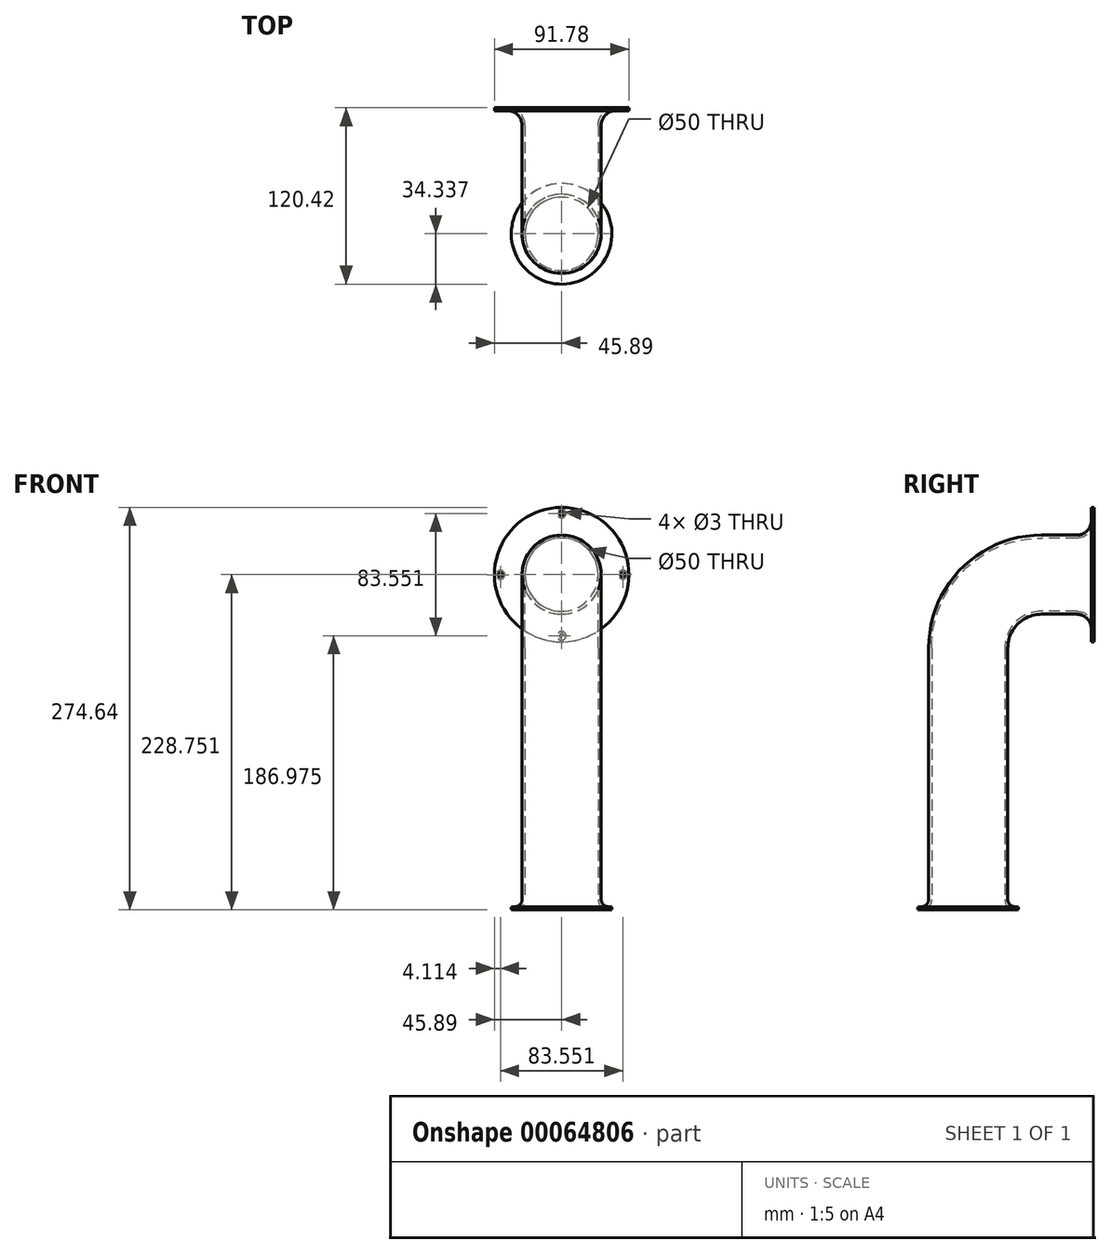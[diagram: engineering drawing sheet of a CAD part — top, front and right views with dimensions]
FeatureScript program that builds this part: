
annotation { "Feature Type Name" : "Feature", "Feature Type Description" : "" }
export const myFeature = defineFeature(function(context is Context, id is Id, definition is map)
    precondition{}
    {
        {
            var Q0;
            Q0=qCreatedBy(makeId("Right.planeOp"),FACE);
            var sketch = newSketch(context, id + "F0", { "sketchPlane" : qUnion([Q0])});
            skLineSegment(sketch, "E0", {"start": v(113.42, 188.16) * mm, "end": v(93.42, 188.16) * mm});
            skLineSegment(sketch, "E1", {"start": v(43.42, 138.16) * mm, "end": v(43.42, -31.84) * mm});
            skPoint(sketch, "E2.visualSharp", {"position": v(43.42, 188.16) * mm});
            skArc(sketch, "E2.filletArc", {"start": v(93.42, 188.16) * mm, "mid": v(58.06, 173.52) * mm, "end": v(43.42, 138.16) * mm});
            skSolve(sketch);
        }
        {
            var Q0;
            Q0=sQuery(id+"F0.wireOp",VERTEX,"E0.start");
            var Q1;
            Q1=sQuery(id+"F0.wireOp",EDGE,"E0");
            cPlane(context, id + "F1", {"entities" : qUnion([Q0, Q1]), "cplaneType" : CPlaneType.LINE_POINT, "offset" : 150 * mm, "width" : 150 * mm, "height" : 150 * mm});
        }
        {
            var Q0;
            Q0=qCreatedBy(id+"F1.planeOp",FACE);
            var sketch = newSketch(context, id + "F2", { "sketchPlane" : qUnion([Q0])});
            skCircle(sketch, "E3", {"center": v(0, 188.16) * mm, "radius": 25 * mm});
            skCircle(sketch, "E4", {"center": v(0, 188.16) * mm, "radius": 27 * mm});
            skPoint(sketch, "E5", {"position": v(0, 163.16) * mm});
            skPoint(sketch, "E6", {"position": v(0, 213.16) * mm});
            skPoint(sketch, "E7", {"position": v(-25, 188.16) * mm});
            skPoint(sketch, "E8", {"position": v(25, 188.16) * mm});
            skPoint(sketch, "E9", {"position": v(-27, 188.16) * mm});
            skPoint(sketch, "E10", {"position": v(27, 188.16) * mm});
            skSolve(sketch);
        }
        {
            var Q0;
            Q0=makeQuery(id+"F2.imprint","IMPRINT",FACE,{"disambiguationData":[TD([[makeQuery(id+"F2.imprint","IMPRINT",EDGE,{"derivedFrom":sQuery(id+"F2.wireOp",EDGE,"E3")}),-1.0]])]});
            var Q1;
            Q1=sQuery(id+"F0.wireOp",EDGE,"E0");
            var Q2;
            Q2=sQuery(id+"F0.wireOp",EDGE,"E2.filletArc");
            var Q3;
            Q3=sQuery(id+"F0.wireOp",EDGE,"E1");
            sweep(context, id + "F3", {"profiles" : qUnion([Q0]), "path" : qUnion([Q1, Q2, Q3])});
        }
        {
            var Q0;
            Q0=sQuery(id+"F2.wireOp",VERTEX,"E5");
            var Q1;
            Q1=sQuery(id+"F2.wireOp",VERTEX,"E6");
            cPlane(context, id + "F4", {"entities" : qUnion([Q0, Q1]), "cplaneType" : CPlaneType.MID_PLANE, "offset" : 150 * mm, "width" : 150 * mm, "height" : 150 * mm});
        }
        {
            var Q0;
            Q0=qCreatedBy(id+"F4.planeOp",FACE);
            var sketch = newSketch(context, id + "F5", { "sketchPlane" : qUnion([Q0])});
            skLineSegment(sketch, "E11", {"start": v(-27, 113.42) * mm, "end": v(-25, 113.42) * mm});
            skLineSegment(sketch, "E12", {"start": v(-27, 113.42) * mm, "end": v(-27, 117.5) * mm});
            skLineSegment(sketch, "E13", {"start": v(-37, 127.5) * mm, "end": v(-38.4, 127.5) * mm});
            skPoint(sketch, "E14.visualSharp", {"position": v(-27, 127.5) * mm});
            skArc(sketch, "E14.filletArc", {"start": v(-27, 117.5) * mm, "mid": v(-29.93, 124.57) * mm, "end": v(-37, 127.5) * mm});
            skArc(sketch, "E15.0", {"start": v(-25, 117.5) * mm, "mid": v(-28.51, 125.98) * mm, "end": v(-37, 129.5) * mm});
            skLineSegment(sketch, "E15.1", {"start": v(-25, 113.42) * mm, "end": v(-25, 117.5) * mm});
            skLineSegment(sketch, "E16", {"start": v(-37, 129.5) * mm, "end": v(-45.9, 129.5) * mm});
            skLineSegment(sketch, "E17", {"start": v(-45.9, 129.5) * mm, "end": v(-45.9, 127.5) * mm});
            skLineSegment(sketch, "E18", {"start": v(-45.9, 127.5) * mm, "end": v(-38.4, 127.5) * mm});
            skLineSegment(sketch, "E19", {"start": v(0, 126.02) * mm, "end": v(0, 107.88) * mm, "construction": true});
            skSolve(sketch);
        }
        {
            var Q0;
            Q0=makeQuery(id+"F5.imprint","IMPRINT",FACE,{"disambiguationData":[TD([[makeQuery(id+"F5.imprint","IMPRINT",EDGE,{"derivedFrom":sQuery(id+"F5.wireOp",EDGE,"E11")}),1.0]])]});
            var Q1;
            Q1=sQuery(id+"F5.wireOp",EDGE,"E19");
            revolve(context, id + "F6", {"operationType" : NewBodyOperationType.ADD, "entities" : qUnion([Q0]), "axis" : qUnion([Q1]), "revolveType" : RevolveType.FULL});
        }
        {
            var Q0;
            Q0=makeQuery(id+"F6.opRevolve","SWEPT_FACE",FACE,{"disambiguationData":[OSD([sQuery(id+"F5.wireOp",EDGE,"E16")])]});
            var sketch = newSketch(context, id + "F7", { "sketchPlane" : qUnion([Q0])});
            skCircle(sketch, "E20", {"center": v(0, 188.16) * mm, "radius": 41.78 * mm, "construction": true});
            skPoint(sketch, "E21", {"position": v(0, 229.94) * mm});
            skPoint(sketch, "E22", {"position": v(0, 146.38) * mm});
            skPoint(sketch, "E23", {"position": v(41.78, 188.1) * mm});
            skPoint(sketch, "E24", {"position": v(-41.78, 188.16) * mm});
            skSolve(sketch);
        }
        {
            var Q0;
            Q0=sQuery(id+"F7.wireOp",VERTEX,"E21");
            var Q1;
            Q1=sQuery(id+"F7.wireOp",VERTEX,"E24");
            var Q2;
            Q2=sQuery(id+"F7.wireOp",VERTEX,"E22");
            var Q3;
            Q3=sQuery(id+"F7.wireOp",VERTEX,"E23");
            var Q4;
            Q4=makeQuery(id+"F3.opSweep","SWEPT_BODY",BODY,{"disambiguationData":[OSD([sQuery(id+"F0.wireOp",EDGE,"E1"),sQuery(id+"F2.wireOp",EDGE,"E3"),sQuery(id+"F2.wireOp",EDGE,"E4")])]});
            hole(context, id + "F8", {"style" : HoleStyle.C_SINK, "holeDiameter" : 3 * mm, "cSinkDiameter" : 6 * mm, "endStyle" : HoleEndStyle.BLIND, "holeDepth" : 5 * mm, "locations" : qUnion([Q0, Q1, Q2, Q3]), "scope" : qUnion([Q4]), "cSinkAngle" : 90 * degree});
        }
        {
            var Q0;
            Q0=makeQuery(id+"F3.opSweep","CAP_FACE",FACE,{"disambiguationData":[OSD([sQuery(id+"F0.wireOp",VERTEX,"E1.end"),sQuery(id+"F2.wireOp",EDGE,"E3"),sQuery(id+"F2.wireOp",EDGE,"E4")])],"isStart":false});
            var sketch = newSketch(context, id + "F9", { "sketchPlane" : qUnion([Q0])});
            skPoint(sketch, "E25", {"position": v(0, -18.42) * mm});
            skPoint(sketch, "E26", {"position": v(0, -68.42) * mm});
            skPoint(sketch, "E27", {"position": v(0, -43.42) * mm});
            skPoint(sketch, "E28", {"position": v(-25, -43.42) * mm});
            skPoint(sketch, "E29", {"position": v(25, -43.42) * mm});
            skPoint(sketch, "E30", {"position": v(27, -43.42) * mm});
            skPoint(sketch, "E31", {"position": v(-27, -43.42) * mm});
            skSolve(sketch);
        }
        {
            var Q0;
            Q0=sQuery(id+"F9.wireOp",VERTEX,"E25");
            var Q1;
            Q1=sQuery(id+"F9.wireOp",VERTEX,"E26");
            cPlane(context, id + "F10", {"entities" : qUnion([Q0, Q1]), "cplaneType" : CPlaneType.MID_PLANE, "offset" : 150 * mm, "width" : 150 * mm, "height" : 150 * mm});
        }
        {
            var Q0;
            Q0=qCreatedBy(id+"F10.planeOp",FACE);
            var sketch = newSketch(context, id + "F11", { "sketchPlane" : qUnion([Q0])});
            skLineSegment(sketch, "E32", {"start": v(-27, -31.84) * mm, "end": v(-27, -33.59) * mm});
            skLineSegment(sketch, "E33", {"start": v(-32, -38.59) * mm, "end": v(-34.34, -38.59) * mm});
            skLineSegment(sketch, "E34", {"start": v(0, -25.1) * mm, "end": v(0, -5.66) * mm, "construction": true});
            skPoint(sketch, "E35.visualSharp", {"position": v(-27, -38.59) * mm});
            skArc(sketch, "E35.filletArc", {"start": v(-32, -38.59) * mm, "mid": v(-28.46, -37.12) * mm, "end": v(-27, -33.59) * mm});
            skLineSegment(sketch, "E36.0", {"start": v(-32, -40.59) * mm, "end": v(-34.34, -40.59) * mm});
            skArc(sketch, "E36.1", {"start": v(-32, -40.59) * mm, "mid": v(-27.05, -38.54) * mm, "end": v(-25, -33.59) * mm});
            skLineSegment(sketch, "E36.2", {"start": v(-25, -31.84) * mm, "end": v(-25, -33.59) * mm});
            skLineSegment(sketch, "E37", {"start": v(-34.34, -40.59) * mm, "end": v(-34.34, -38.59) * mm});
            skLineSegment(sketch, "E38", {"start": v(-27, -31.84) * mm, "end": v(-25, -31.84) * mm});
            skSolve(sketch);
        }
        {
            var Q0;
            Q0 = qSketchRegion(id + "F11", true);
            var Q1;
            Q1=sQuery(id+"F11.wireOp",EDGE,"E34");
            revolve(context, id + "F12", {"operationType" : NewBodyOperationType.ADD, "entities" : qUnion([Q0]), "axis" : qUnion([Q1]), "revolveType" : RevolveType.FULL});
        }
    });
